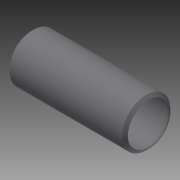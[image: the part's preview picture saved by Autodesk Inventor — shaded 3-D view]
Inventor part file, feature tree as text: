
AUTODESK INVENTOR PART (.ipt)
format: ipt  version: 2014 (Build 180170000, 170)  size: 129,536 bytes
history: native  units: in
note: dims shown in document units (in); Inventor stores cm internally (conversion verified against a paired STEP export)
features: other x56, revolve x1, sketch x1
ambient origin geometry x8: Origin, YZ Plane, XZ Plane, XY Plane, X Axis, Y Axis, Z Axis, Center Point
bodies: Solid1 (feature_tree)
feature tree (58):
  revolve  "Revolution1"  [1 undecoded]
  other  "o1_XY"
  other  "o1_YZ"
  other  "o1_ZX"
  other  "o1_X"
  other  "o1_Y"
  other  "o1_Z"
  other  "o1_Center"
  other  "o2_XY"
  other  "o2_YZ"
  other  "o2_ZX"
  other  "o2_X"
  other  "o2_Y"
  other  "o2_Z"
  other  "o2_Center"
  other  "t1_XY"
  other  "t1_YZ"
  other  "t1_ZX"
  other  "t1_X"
  other  "t1_Y"
  other  "t1_Z"
  other  "t1_Center"
  other  "t2_XY"
  other  "t2_YZ"
  other  "t2_ZX"
  other  "t2_X"
  other  "t2_Y"
  other  "t2_Z"
  other  "t2_Center"
  other  "t3_XY"
  other  "t3_YZ"
  other  "t3_ZX"
  other  "t3_X"
  other  "t3_Y"
  other  "t3_Z"
  other  "t3_Center"
  other  "t4_XY"
  other  "t4_YZ"
  other  "t4_ZX"
  other  "t4_X"
  other  "t4_Y"
  other  "t4_Z"
  other  "t4_Center"
  other  "tube1_XY"
  other  "tube1_YZ"
  other  "tube1_ZX"
  other  "tube1_X"
  other  "tube1_Y"
  other  "tube1_Z"
  other  "tube1_Center"
  other  "tube2_XY"
  other  "tube2_YZ"
  other  "tube2_ZX"
  other  "tube2_X"
  other  "tube2_Y"
  other  "tube2_Z"
  other  "tube2_Center"
  sketch  "Sketch_5"  dims[d0=360.0deg]
note: 1 required parameter value undecoded (feature->parameter linkage not recoverable at this tier; creation-order binding heuristic only, values carry confidence <= 0.55)
